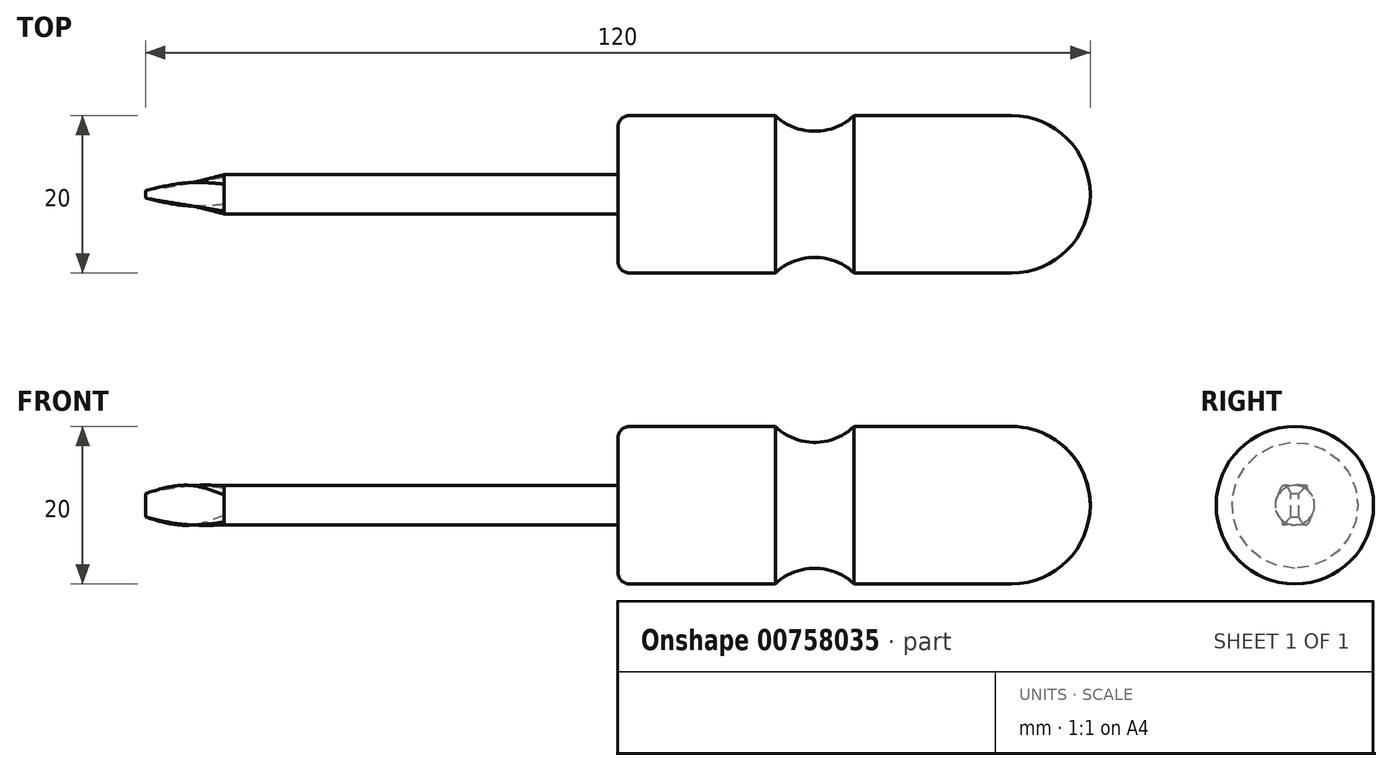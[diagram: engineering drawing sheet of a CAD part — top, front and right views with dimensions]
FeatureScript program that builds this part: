
annotation { "Feature Type Name" : "Feature", "Feature Type Description" : "" }
export const myFeature = defineFeature(function(context is Context, id is Id, definition is map)
    precondition{}
    {
        {
            var Q0;
            Q0=qCreatedBy(makeId("Front.planeOp"),FACE);
            var sketch = newSketch(context, id + "F0", { "sketchPlane" : qUnion([Q0])});
            skLineSegment(sketch, "E0", {"start": v(-22.1, 0) * mm, "end": v(27.1, 0) * mm, "construction": true});
            skLineSegment(sketch, "E1", {"start": v(2.4, 0) * mm, "end": v(2.4, 10) * mm, "construction": true});
            skLineSegment(sketch, "E2", {"start": v(2.4, 10) * mm, "end": v(22.4, 10) * mm});
            skArc(sketch, "E3", {"start": v(22.4, 10) * mm, "mid": v(29.47, 7.07) * mm, "end": v(32.4, 0) * mm});
            skLineSegment(sketch, "E4", {"start": v(32.4, 0) * mm, "end": v(-27.6, 0) * mm});
            skLineSegment(sketch, "E5", {"start": v(-27.6, 0) * mm, "end": v(-27.6, 10) * mm});
            skLineSegment(sketch, "E6", {"start": v(-27.6, 10) * mm, "end": v(-7.6, 10) * mm});
            skLineSegment(sketch, "E7", {"start": v(-7.6, 10) * mm, "end": v(2.4, 10) * mm, "construction": true});
            skLineSegment(sketch, "E8", {"start": v(-2.6, 10) * mm, "end": v(-2.6, 8) * mm, "construction": true});
            skArc(sketch, "E9", {"start": v(-7.6, 10) * mm, "mid": v(-2.6, 8) * mm, "end": v(2.4, 10) * mm});
            skSolve(sketch);
        }
        {
            var Q0;
            Q0=makeQuery(id+"F0.imprint","IMPRINT",FACE,{"disambiguationData":[TD([[makeQuery(id+"F0.imprint","IMPRINT",EDGE,{"derivedFrom":sQuery(id+"F0.wireOp",EDGE,"E2")}),-1.0]])]});
            var Q1;
            Q1=sQuery(id+"F0.wireOp",EDGE,"E4");
            revolve(context, id + "F1", {"surfaceOperationType" : NewSurfaceOperationType.NEW, "entities" : qUnion([Q0]), "axis" : qUnion([Q1]), "revolveType" : RevolveType.FULL});
        }
        {
            var Q0;
            Q0=makeQuery(id+"F1.opRevolve","SWEPT_FACE",FACE,{"disambiguationData":[OSD([sQuery(id+"F0.wireOp",EDGE,"E5")])]});
            var sketch = newSketch(context, id + "F2", { "sketchPlane" : qUnion([Q0])});
            skCircle(sketch, "E10", {"center": v(0, 0) * mm, "radius": 2.5 * mm});
            skSolve(sketch);
        }
        {
            var Q0;
            Q0=makeQuery(id+"F2.imprint","IMPRINT",FACE,{"disambiguationData":[TD([[makeQuery(id+"F2.imprint","IMPRINT",EDGE,{"derivedFrom":sQuery(id+"F2.wireOp",EDGE,"E10")}),1.0]])]});
            extrude(context, id + "F3", {"entities" : qUnion([Q0]), "operationType" : NewBodyOperationType.ADD, "depth" : 50 * mm, "offsetDistance" : 25 * mm});
        }
        {
            var Q0;
            Q0=makeQuery(id+"F1.opRevolve","SWEPT_EDGE",EDGE,{"disambiguationData":[OSD([sQuery(id+"F0.wireOp",EDGE,"E5"),sQuery(id+"F0.wireOp",EDGE,"E6")])]});
            fillet(context, id + "F4", {"entities" : qUnion([Q0]), "radius" : 1.5 * mm, "tangentPropagation" : true, "allowEdgeOverflow" : false});
        }
        {
            var Q0;
            Q0=makeQuery(id+"F3.opExtrude","CAP_FACE",FACE,{"disambiguationData":[OSD([sQuery(id+"F2.wireOp",EDGE,"E10")])],"isStart":false});
            cPlane(context, id + "F5", {"entities" : qUnion([Q0]), "cplaneType" : CPlaneType.OFFSET, "offset" : 4 * mm, "width" : 150 * mm, "height" : 150 * mm});
        }
        {
            var Q0;
            Q0=qCreatedBy(id+"F5.planeOp",FACE);
            cPlane(context, id + "F6", {"entities" : qUnion([Q0]), "cplaneType" : CPlaneType.OFFSET, "offset" : 6 * mm, "width" : 150 * mm, "height" : 150 * mm});
        }
        {
            var Q0;
            Q0=qCreatedBy(id+"F5.planeOp",FACE);
            var sketch = newSketch(context, id + "F7", { "sketchPlane" : qUnion([Q0])});
            skLineSegment(sketch, "E11.bottom", {"start": v(1.5, -2.5) * mm, "end": v(-1.5, -2.5) * mm});
            skLineSegment(sketch, "E11.top", {"start": v(1.5, 2.5) * mm, "end": v(-1.5, 2.5) * mm});
            skLineSegment(sketch, "E11.left", {"start": v(1.5, -2.5) * mm, "end": v(1.5, 2.5) * mm});
            skLineSegment(sketch, "E11.right", {"start": v(-1.5, -2.5) * mm, "end": v(-1.5, 2.5) * mm});
            skPoint(sketch, "E11.middle", {"position": v(0, 0) * mm});
            skSolve(sketch);
        }
        {
            var Q0;
            Q0=qCreatedBy(id+"F6.planeOp",FACE);
            var sketch = newSketch(context, id + "F8", { "sketchPlane" : qUnion([Q0])});
            skLineSegment(sketch, "E12.0.0", {"start": v(1.5, -2.5) * mm, "end": v(1.5, 2.5) * mm, "construction": true});
            skLineSegment(sketch, "E12.0.1", {"start": v(1.5, 2.5) * mm, "end": v(-1.5, 2.5) * mm, "construction": true});
            skLineSegment(sketch, "E12.0.2", {"start": v(-1.5, 2.5) * mm, "end": v(-1.5, -2.5) * mm, "construction": true});
            skLineSegment(sketch, "E12.0.3", {"start": v(-1.5, -2.5) * mm, "end": v(1.5, -2.5) * mm, "construction": true});
            skLineSegment(sketch, "E13.0", {"start": v(0.5, -1.5) * mm, "end": v(0.5, 1.5) * mm});
            skLineSegment(sketch, "E13.1", {"start": v(0.5, -1.5) * mm, "end": v(-0.5, -1.5) * mm});
            skLineSegment(sketch, "E13.2", {"start": v(-0.5, -1.5) * mm, "end": v(-0.5, 1.5) * mm});
            skLineSegment(sketch, "E13.3", {"start": v(0.5, 1.5) * mm, "end": v(-0.5, 1.5) * mm});
            skLineSegment(sketch, "E14.0", {"start": v(6.5, -7.5) * mm, "end": v(6.5, 7.5) * mm});
            skLineSegment(sketch, "E14.1", {"start": v(-6.5, -7.5) * mm, "end": v(6.5, -7.5) * mm});
            skLineSegment(sketch, "E14.2", {"start": v(-6.5, 7.5) * mm, "end": v(-6.5, -7.5) * mm});
            skLineSegment(sketch, "E14.3", {"start": v(6.5, 7.5) * mm, "end": v(-6.5, 7.5) * mm});
            skSolve(sketch);
        }
        {
            var Q0;
            Q0=makeQuery(id+"F3.opExtrude","CAP_FACE",FACE,{"disambiguationData":[OSD([sQuery(id+"F2.wireOp",EDGE,"E10")])],"isStart":false});
            var Q1;
            Q1=makeQuery(id+"F7.imprint","IMPRINT",FACE,{"disambiguationData":[TD([[makeQuery(id+"F7.imprint","IMPRINT",EDGE,{"derivedFrom":sQuery(id+"F7.wireOp",EDGE,"E11.bottom")}),-1.0]])]});
            var Q2;
            Q2=makeQuery(id+"F8.imprint","IMPRINT",FACE,{"disambiguationData":[TD([[makeQuery(id+"F8.imprint","IMPRINT",EDGE,{"derivedFrom":sQuery(id+"F8.wireOp",EDGE,"E13.0")}),1.0]])]});
            loft(context, id + "F9", {"operationType" : NewBodyOperationType.ADD, "sheetProfilesArray" : [{ "sheetProfileEntities" : qUnion([Q0]) }, { "sheetProfileEntities" : qUnion([Q1]) }, { "sheetProfileEntities" : qUnion([Q2]) }]});
        }
    });
